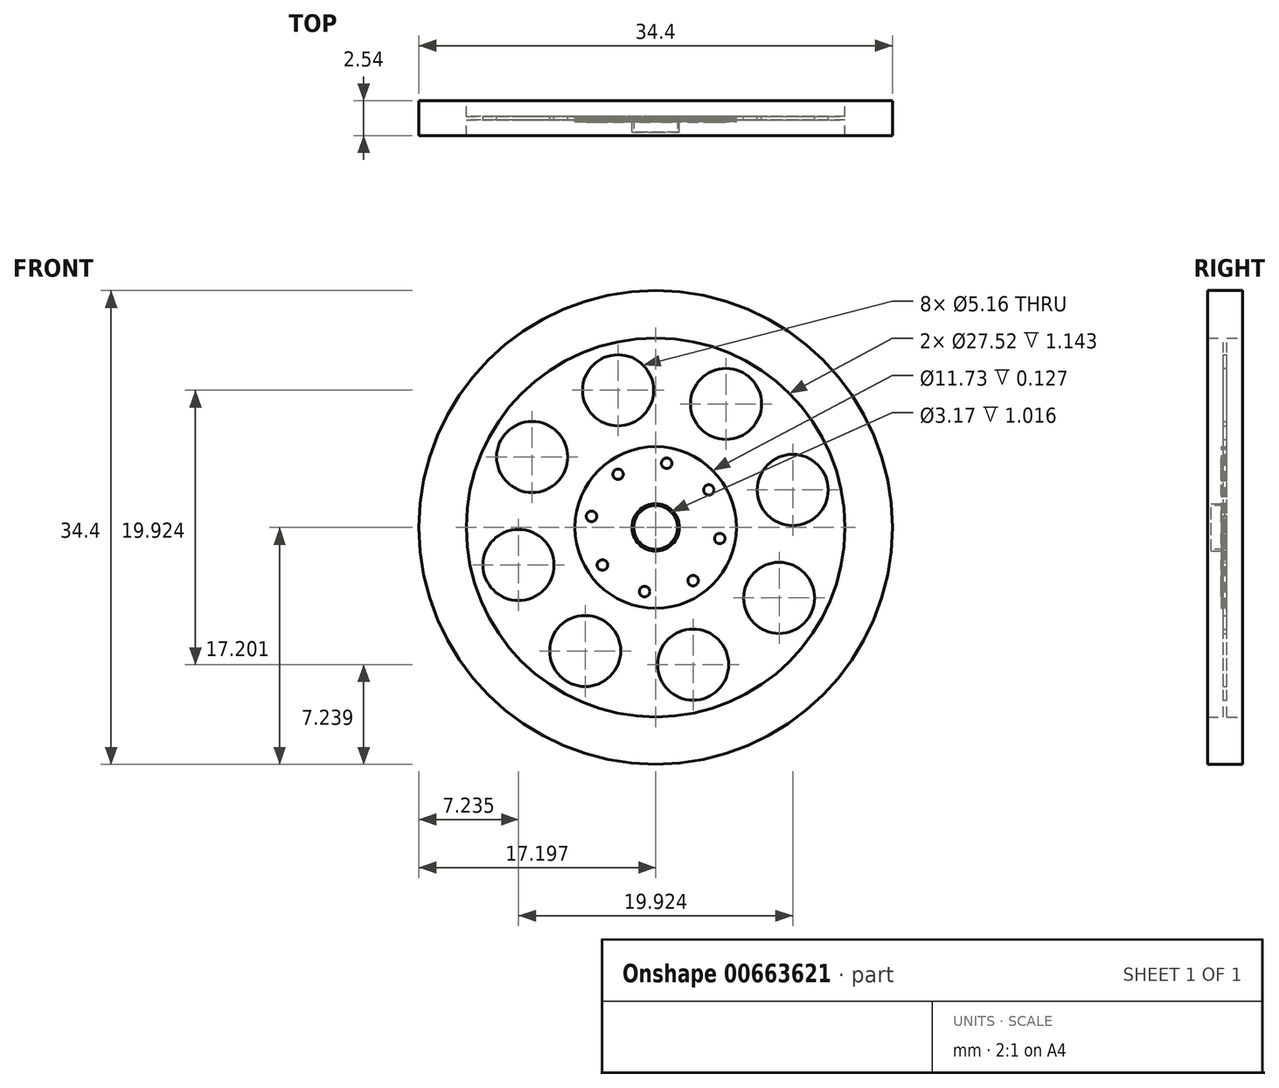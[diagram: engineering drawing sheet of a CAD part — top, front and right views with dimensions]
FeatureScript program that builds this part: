
annotation { "Feature Type Name" : "Feature", "Feature Type Description" : "" }
export const myFeature = defineFeature(function(context is Context, id is Id, definition is map)
    precondition{}
    {
        {
            var Q0;
            Q0=qCreatedBy(makeId("Front.planeOp"),FACE);
            var sketch = newSketch(context, id + "F0", { "sketchPlane" : qUnion([Q0])});
            skCircle(sketch, "E0", {"center": v(-22.67, 24.88) * mm, "radius": 17.2 * mm});
            skCircle(sketch, "E1", {"center": v(-22.67, 24.88) * mm, "radius": 13.76 * mm});
            skCircle(sketch, "E2", {"center": v(-22.67, 24.88) * mm, "radius": 5.86 * mm});
            skCircle(sketch, "E3", {"center": v(-22.67, 24.88) * mm, "radius": 1.72 * mm});
            skCircle(sketch, "E4", {"center": v(-25.4, 34.84) * mm, "radius": 2.58 * mm});
            skCircle(sketch, "E5.1.0", {"center": v(-31.65, 30) * mm, "radius": 2.58 * mm});
            skCircle(sketch, "E5.2.0", {"center": v(-32.63, 22.15) * mm, "radius": 2.58 * mm});
            skCircle(sketch, "E5.3.0", {"center": v(-27.79, 15.9) * mm, "radius": 2.58 * mm});
            skCircle(sketch, "E5.4.0", {"center": v(-19.95, 14.92) * mm, "radius": 2.58 * mm});
            skCircle(sketch, "E5.5.0", {"center": v(-13.7, 19.76) * mm, "radius": 2.58 * mm});
            skCircle(sketch, "E5.6.0", {"center": v(-12.71, 27.6) * mm, "radius": 2.58 * mm});
            skCircle(sketch, "E5.7.0", {"center": v(-17.56, 33.85) * mm, "radius": 2.58 * mm});
            skCircle(sketch, "E6", {"center": v(-25.4, 28.74) * mm, "radius": 0.38 * mm});
            skCircle(sketch, "E7.1.0", {"center": v(-27.33, 25.68) * mm, "radius": 0.38 * mm});
            skCircle(sketch, "E7.2.0", {"center": v(-26.54, 22.15) * mm, "radius": 0.38 * mm});
            skCircle(sketch, "E7.3.0", {"center": v(-23.48, 20.22) * mm, "radius": 0.38 * mm});
            skCircle(sketch, "E7.4.0", {"center": v(-19.95, 21.02) * mm, "radius": 0.38 * mm});
            skCircle(sketch, "E7.5.0", {"center": v(-18.01, 24.08) * mm, "radius": 0.38 * mm});
            skCircle(sketch, "E7.6.0", {"center": v(-18.8, 27.6) * mm, "radius": 0.38 * mm});
            skCircle(sketch, "E7.7.0", {"center": v(-21.87, 29.54) * mm, "radius": 0.38 * mm});
            skPoint(sketch, "E8.first.point", {"position": v(-31.09, 35.18) * mm});
            skPoint(sketch, "E8.second.point", {"position": v(-31.16, 35.71) * mm});
            skPoint(sketch, "E8.third.point", {"position": v(-17.62, 12.08) * mm});
            skPoint(sketch, "E9.second.point", {"position": v(-26.3, 38.15) * mm});
            skPoint(sketch, "E9.third.point", {"position": v(-14.19, 35.71) * mm});
            skSolve(sketch);
        }
        {
            var Q0;
            Q0=makeQuery(id+"F0.imprint","IMPRINT",FACE,{"disambiguationData":[TD([[makeQuery(id+"F0.imprint","IMPRINT",EDGE,{"derivedFrom":sQuery(id+"F0.wireOp",EDGE,"E3")}),1.0]])]});
            extrude(context, id + "F1", {"entities" : qUnion([Q0]), "depth" : 1.02 * mm, "offsetDistance" : 25.4 * mm});
        }
        {
            var Q0;
            Q0=makeQuery(id+"F0.imprint","IMPRINT",FACE,{"disambiguationData":[TD([[makeQuery(id+"F0.imprint","IMPRINT",EDGE,{"derivedFrom":sQuery(id+"F0.wireOp",EDGE,"E2")}),1.0]])]});
            extrude(context, id + "F2", {"entities" : qUnion([Q0]), "operationType" : NewBodyOperationType.ADD, "depth" : 0.25 * mm, "offsetDistance" : 25.4 * mm});
        }
        {
            var Q0;
            Q0=makeQuery(id+"F0.imprint","IMPRINT",FACE,{"disambiguationData":[TD([[makeQuery(id+"F0.imprint","IMPRINT",EDGE,{"derivedFrom":sQuery(id+"F0.wireOp",EDGE,"E7.3.0")}),1.0]])]});
            var Q1;
            Q1=makeQuery(id+"F0.imprint","IMPRINT",FACE,{"disambiguationData":[TD([[makeQuery(id+"F0.imprint","IMPRINT",EDGE,{"derivedFrom":sQuery(id+"F0.wireOp",EDGE,"E7.4.0")}),1.0]])]});
            var Q2;
            Q2=makeQuery(id+"F0.imprint","IMPRINT",FACE,{"disambiguationData":[TD([[makeQuery(id+"F0.imprint","IMPRINT",EDGE,{"derivedFrom":sQuery(id+"F0.wireOp",EDGE,"E7.5.0")}),1.0]])]});
            var Q3;
            Q3=makeQuery(id+"F0.imprint","IMPRINT",FACE,{"disambiguationData":[TD([[makeQuery(id+"F0.imprint","IMPRINT",EDGE,{"derivedFrom":sQuery(id+"F0.wireOp",EDGE,"E7.6.0")}),1.0]])]});
            var Q4;
            Q4=makeQuery(id+"F0.imprint","IMPRINT",FACE,{"disambiguationData":[TD([[makeQuery(id+"F0.imprint","IMPRINT",EDGE,{"derivedFrom":sQuery(id+"F0.wireOp",EDGE,"E7.7.0")}),1.0]])]});
            var Q5;
            Q5=makeQuery(id+"F0.imprint","IMPRINT",FACE,{"disambiguationData":[TD([[makeQuery(id+"F0.imprint","IMPRINT",EDGE,{"derivedFrom":sQuery(id+"F0.wireOp",EDGE,"E6")}),1.0]])]});
            var Q6;
            Q6=makeQuery(id+"F0.imprint","IMPRINT",FACE,{"disambiguationData":[TD([[makeQuery(id+"F0.imprint","IMPRINT",EDGE,{"derivedFrom":sQuery(id+"F0.wireOp",EDGE,"E7.1.0")}),1.0]])]});
            var Q7;
            Q7=makeQuery(id+"F0.imprint","IMPRINT",FACE,{"disambiguationData":[TD([[makeQuery(id+"F0.imprint","IMPRINT",EDGE,{"derivedFrom":sQuery(id+"F0.wireOp",EDGE,"E7.2.0")}),1.0]])]});
            extrude(context, id + "F3", {"entities" : qUnion([Q0, Q1, Q2, Q3, Q4, Q5, Q6, Q7]), "operationType" : NewBodyOperationType.ADD, "depth" : 0.28 * mm, "offsetDistance" : 25.4 * mm});
        }
        {
            var Q0;
            Q0=makeQuery(id+"F0.imprint","IMPRINT",FACE,{"disambiguationData":[TD([[makeQuery(id+"F0.imprint","IMPRINT",EDGE,{"derivedFrom":sQuery(id+"F0.wireOp",EDGE,"E0")}),1.0]])]});
            extrude(context, id + "F4", {"entities" : qUnion([Q0]), "operationType" : NewBodyOperationType.ADD, "endBound" : BoundingType.SYMMETRIC, "depth" : 2.54 * mm, "offsetDistance" : 25.4 * mm});
        }
        {
            var Q0;
            Q0=makeQuery(id+"F0.imprint","IMPRINT",FACE,{"disambiguationData":[TD([[makeQuery(id+"F0.imprint","IMPRINT",EDGE,{"derivedFrom":sQuery(id+"F0.wireOp",EDGE,"E2")}),-1.0]])]});
            extrude(context, id + "F5", {"entities" : qUnion([Q0]), "operationType" : NewBodyOperationType.ADD, "endBound" : BoundingType.SYMMETRIC, "depth" : 0.25 * mm, "offsetDistance" : 25.4 * mm});
        }
        {
            var Q0;
            Q0=makeQuery(id+"F1.opExtrude","CAP_FACE",FACE,{"disambiguationData":[OSD([sQuery(id+"F0.wireOp",EDGE,"E3")])],"isStart":false});
            var sketch = newSketch(context, id + "F6", { "sketchPlane" : qUnion([Q0])});
            skCircle(sketch, "E10", {"center": v(-22.67, 24.88) * mm, "radius": 1.59 * mm});
            skSolve(sketch);
        }
        {
            var Q0;
            Q0 = qSketchRegion(id + "F6", true);
            extrude(context, id + "F7", {"entities" : qUnion([Q0]), "operationType" : NewBodyOperationType.REMOVE, "oppositeDirection" : true, "depth" : 25.4 * mm, "offsetDistance" : 25.4 * mm});
        }
    });
